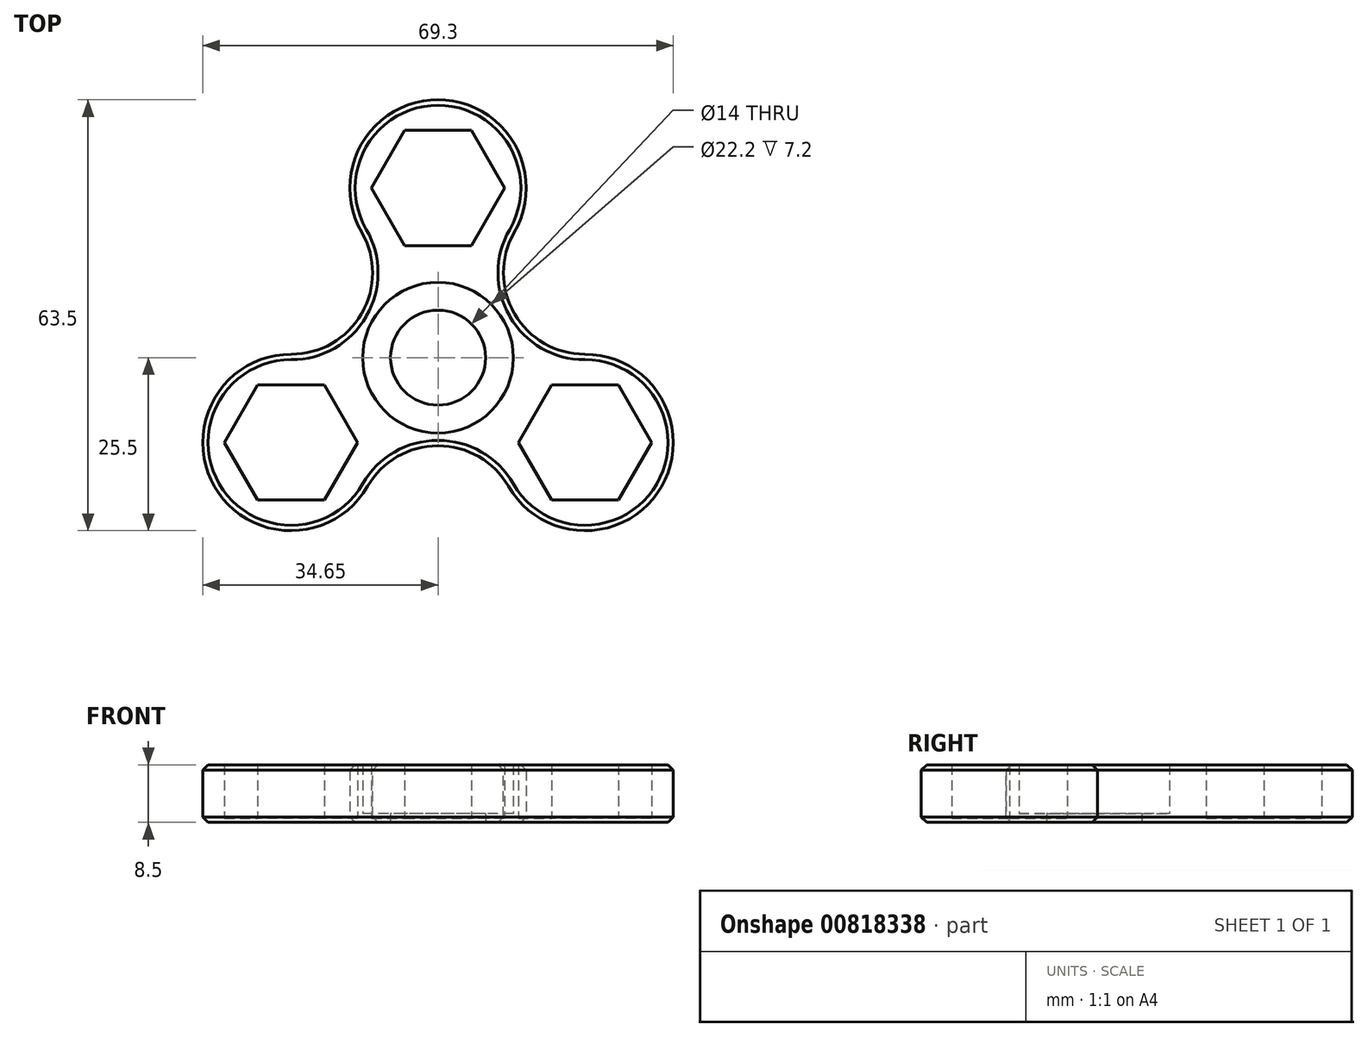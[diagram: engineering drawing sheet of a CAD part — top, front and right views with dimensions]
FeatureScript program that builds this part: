
annotation { "Feature Type Name" : "Feature", "Feature Type Description" : "" }
export const myFeature = defineFeature(function(context is Context, id is Id, definition is map)
    precondition{}
    {
        {
            var Q0;
            Q0=qCreatedBy(makeId("Top.planeOp"),FACE);
            var sketch = newSketch(context, id + "F0", { "sketchPlane" : qUnion([Q0])});
            skCircle(sketch, "E0", {"center": v(0, 0) * mm, "radius": 13 * mm});
            skCircle(sketch, "E1", {"center": v(0, 0) * mm, "radius": 11.1 * mm});
            skCircle(sketch, "E2", {"center": v(0, 25) * mm, "radius": 13 * mm});
            skCircle(sketch, "E3.cCircle", {"center": v(0, 25) * mm, "radius": 8.5 * mm, "construction": true});
            skLineSegment(sketch, "E3.0", {"start": v(9.81, 25) * mm, "end": v(4.9, 16.5) * mm});
            skLineSegment(sketch, "E3.1", {"start": v(4.9, 16.5) * mm, "end": v(-4.9, 16.5) * mm});
            skLineSegment(sketch, "E3.2", {"start": v(-4.9, 16.5) * mm, "end": v(-9.81, 25) * mm});
            skLineSegment(sketch, "E3.3", {"start": v(-9.81, 25) * mm, "end": v(-4.9, 33.5) * mm});
            skLineSegment(sketch, "E3.4", {"start": v(-4.9, 33.5) * mm, "end": v(4.9, 33.5) * mm});
            skLineSegment(sketch, "E3.5", {"start": v(4.9, 33.5) * mm, "end": v(9.81, 25) * mm});
            skPoint(sketch, "E3.0.midPoint", {"position": v(7.36, 20.75) * mm});
            skCircle(sketch, "E4", {"center": v(0, 0) * mm, "radius": 7 * mm});
            skCircle(sketch, "E5.1.0", {"center": v(-21.65, -12.5) * mm, "radius": 13 * mm});
            skLineSegment(sketch, "E5.1.1", {"start": v(-16.74, -4) * mm, "end": v(-11.84, -12.5) * mm});
            skLineSegment(sketch, "E5.1.2", {"start": v(-26.56, -4) * mm, "end": v(-16.74, -4) * mm});
            skLineSegment(sketch, "E5.1.3", {"start": v(-31.47, -12.5) * mm, "end": v(-26.56, -4) * mm});
            skLineSegment(sketch, "E5.1.4", {"start": v(-26.56, -21) * mm, "end": v(-31.47, -12.5) * mm});
            skLineSegment(sketch, "E5.1.5", {"start": v(-16.74, -21) * mm, "end": v(-26.56, -21) * mm});
            skLineSegment(sketch, "E5.1.6", {"start": v(-11.84, -12.5) * mm, "end": v(-16.74, -21) * mm});
            skCircle(sketch, "E5.2.0", {"center": v(21.65, -12.5) * mm, "radius": 13 * mm});
            skLineSegment(sketch, "E5.2.1", {"start": v(11.84, -12.5) * mm, "end": v(16.74, -4) * mm});
            skLineSegment(sketch, "E5.2.2", {"start": v(16.74, -21) * mm, "end": v(11.84, -12.5) * mm});
            skLineSegment(sketch, "E5.2.3", {"start": v(26.56, -21) * mm, "end": v(16.74, -21) * mm});
            skLineSegment(sketch, "E5.2.4", {"start": v(31.47, -12.5) * mm, "end": v(26.56, -21) * mm});
            skLineSegment(sketch, "E5.2.5", {"start": v(26.56, -4) * mm, "end": v(31.47, -12.5) * mm});
            skLineSegment(sketch, "E5.2.6", {"start": v(16.74, -4) * mm, "end": v(26.56, -4) * mm});
            skSolve(sketch);
        }
        {
            var Q0;
            Q0=makeQuery(id+"F0.imprint","IMPRINT",FACE,{"disambiguationData":[TD([[makeQuery(id+"F0.imprint","IMPRINT",EDGE,{"derivedFrom":sQuery(id+"F0.wireOp",EDGE,"E3.0")}),1.0]])]});
            var Q1;
            Q1=makeQuery(id+"F0.imprint","IMPRINT",FACE,{"disambiguationData":[TD([[makeQuery(id+"F0.imprint","IMPRINT",EDGE,{"derivedFrom":sQuery(id+"F0.wireOp",EDGE,"E3.0")}),-1.0]])]});
            var Q2;
            Q2=makeQuery(id+"F0.imprint","IMPRINT",FACE,{"disambiguationData":[TD([[makeQuery(id+"F0.imprint","IMPRINT",EDGE,{"derivedFrom":sQuery(id+"F0.wireOp",EDGE,"E1")}),1.0]])]});
            var Q3;
            Q3=makeQuery(id+"F0.imprint","IMPRINT",FACE,{"disambiguationData":[TD([[makeQuery(id+"F0.imprint","IMPRINT",EDGE,{"derivedFrom":sQuery(id+"F0.wireOp",EDGE,"E1")}),-1.0]])]});
            var Q4;
            {var subQ0=sQuery(id+"F0.wireOp",EDGE,"E2");var subQ1=sQuery(id+"F0.wireOp",EDGE,"E0");var subQ2=makeQuery(id+"F0.imprint","INTERSECT",VERTEX,{"disambiguationData":[OD(0.0)],"derivedFrom":[subQ1,subQ0]});Q4=makeQuery(id+"F0.imprint","IMPRINT",FACE,{"disambiguationData":[TD([[makeQuery(id+"F0.imprint","IMPRINT",EDGE,{"disambiguationData":[TD([[subQ2,1.0]])],"derivedFrom":subQ1}),1.0]])]});}
            var Q5;
            {var subQ0=sQuery(id+"F0.wireOp",EDGE,"d04d9439-d31e-4a44-955d-4c44843ed1f90.MirrorC");var subQ1=sQuery(id+"F0.wireOp",EDGE,"E0");var subQ2=makeQuery(id+"F0.imprint","INTERSECT",VERTEX,{"disambiguationData":[OD(0.0)],"derivedFrom":[subQ1,subQ0]});Q5=makeQuery(id+"F0.imprint","IMPRINT",FACE,{"disambiguationData":[TD([[makeQuery(id+"F0.imprint","IMPRINT",EDGE,{"disambiguationData":[TD([[subQ2,-1.0]])],"derivedFrom":subQ1}),1.0]])]});}
            var Q6;
            Q6=makeQuery(id+"F0.imprint","IMPRINT",FACE,{"disambiguationData":[TD([[makeQuery(id+"F0.imprint","IMPRINT",EDGE,{"derivedFrom":sQuery(id+"F0.wireOp",EDGE,"235c1c98-600d-46e9-b86c-8ce5ef518ee80.MirrorCS")}),-1.0]])]});
            var Q7;
            Q7=makeQuery(id+"F0.imprint","IMPRINT",FACE,{"disambiguationData":[TD([[makeQuery(id+"F0.imprint","IMPRINT",EDGE,{"derivedFrom":sQuery(id+"F0.wireOp",EDGE,"235c1c98-600d-46e9-b86c-8ce5ef518ee80.MirrorCS")}),1.0]])]});
            var Q8;
            Q8=makeQuery(id+"F0.imprint","IMPRINT",FACE,{"disambiguationData":[TD([[makeQuery(id+"F0.imprint","IMPRINT",EDGE,{"derivedFrom":sQuery(id+"F0.wireOp",EDGE,"E5.1.1")}),1.0]])]});
            var Q9;
            Q9=makeQuery(id+"F0.imprint","IMPRINT",FACE,{"disambiguationData":[TD([[makeQuery(id+"F0.imprint","IMPRINT",EDGE,{"derivedFrom":sQuery(id+"F0.wireOp",EDGE,"E5.2.1")}),1.0]])]});
            var Q10;
            Q10=makeQuery(id+"F0.imprint","IMPRINT",FACE,{"disambiguationData":[TD([[makeQuery(id+"F0.imprint","IMPRINT",EDGE,{"derivedFrom":sQuery(id+"F0.wireOp",EDGE,"E5.1.1")}),-1.0]])]});
            var Q11;
            Q11=makeQuery(id+"F0.imprint","IMPRINT",FACE,{"disambiguationData":[TD([[makeQuery(id+"F0.imprint","IMPRINT",EDGE,{"derivedFrom":sQuery(id+"F0.wireOp",EDGE,"E5.2.1")}),-1.0]])]});
            var Q12;
            {var subQ0=sQuery(id+"F0.wireOp",EDGE,"E5.1.0");var subQ1=sQuery(id+"F0.wireOp",EDGE,"E0");var subQ2=makeQuery(id+"F0.imprint","INTERSECT",VERTEX,{"disambiguationData":[OD(0.0)],"derivedFrom":[subQ1,subQ0]});Q12=makeQuery(id+"F0.imprint","IMPRINT",FACE,{"disambiguationData":[TD([[makeQuery(id+"F0.imprint","IMPRINT",EDGE,{"disambiguationData":[TD([[subQ2,-1.0]])],"derivedFrom":subQ1}),1.0]])]});}
            var Q13;
            {var subQ0=sQuery(id+"F0.wireOp",EDGE,"E5.2.0");var subQ1=sQuery(id+"F0.wireOp",EDGE,"E0");var subQ2=makeQuery(id+"F0.imprint","INTERSECT",VERTEX,{"disambiguationData":[OD(0.0)],"derivedFrom":[subQ1,subQ0]});Q13=makeQuery(id+"F0.imprint","IMPRINT",FACE,{"disambiguationData":[TD([[makeQuery(id+"F0.imprint","IMPRINT",EDGE,{"disambiguationData":[TD([[subQ2,-1.0]])],"derivedFrom":subQ1}),1.0]])]});}
            extrude(context, id + "F1", {"entities" : qUnion([Q0, Q1, Q2, Q3, Q4, Q5, Q6, Q7, Q8, Q9, Q10, Q11, Q12, Q13]), "depth" : 0.6 * mm, "offsetDistance" : 25 * mm});
        }
        {
            var Q0;
            Q0=makeQuery(id+"F0.imprint","IMPRINT",FACE,{"disambiguationData":[TD([[makeQuery(id+"F0.imprint","IMPRINT",EDGE,{"derivedFrom":sQuery(id+"F0.wireOp",EDGE,"E3.0")}),1.0]])]});
            var Q1;
            Q1=makeQuery(id+"F0.imprint","IMPRINT",FACE,{"disambiguationData":[TD([[makeQuery(id+"F0.imprint","IMPRINT",EDGE,{"derivedFrom":sQuery(id+"F0.wireOp",EDGE,"E1")}),-1.0]])]});
            var Q2;
            {var subQ0=sQuery(id+"F0.wireOp",EDGE,"E2");var subQ1=sQuery(id+"F0.wireOp",EDGE,"E0");var subQ2=makeQuery(id+"F0.imprint","INTERSECT",VERTEX,{"disambiguationData":[OD(0.0)],"derivedFrom":[subQ1,subQ0]});Q2=makeQuery(id+"F0.imprint","IMPRINT",FACE,{"disambiguationData":[TD([[makeQuery(id+"F0.imprint","IMPRINT",EDGE,{"disambiguationData":[TD([[subQ2,1.0]])],"derivedFrom":subQ1}),1.0]])]});}
            var Q3;
            {var subQ0=sQuery(id+"F0.wireOp",EDGE,"d04d9439-d31e-4a44-955d-4c44843ed1f90.MirrorC");var subQ1=sQuery(id+"F0.wireOp",EDGE,"E0");var subQ2=makeQuery(id+"F0.imprint","INTERSECT",VERTEX,{"disambiguationData":[OD(0.0)],"derivedFrom":[subQ1,subQ0]});Q3=makeQuery(id+"F0.imprint","IMPRINT",FACE,{"disambiguationData":[TD([[makeQuery(id+"F0.imprint","IMPRINT",EDGE,{"disambiguationData":[TD([[subQ2,-1.0]])],"derivedFrom":subQ1}),1.0]])]});}
            var Q4;
            Q4=makeQuery(id+"F0.imprint","IMPRINT",FACE,{"disambiguationData":[TD([[makeQuery(id+"F0.imprint","IMPRINT",EDGE,{"derivedFrom":sQuery(id+"F0.wireOp",EDGE,"235c1c98-600d-46e9-b86c-8ce5ef518ee80.MirrorCS")}),-1.0]])]});
            var Q5;
            Q5=makeQuery(id+"F0.imprint","IMPRINT",FACE,{"disambiguationData":[TD([[makeQuery(id+"F0.imprint","IMPRINT",EDGE,{"derivedFrom":sQuery(id+"F0.wireOp",EDGE,"E5.1.1")}),1.0]])]});
            var Q6;
            {var subQ0=sQuery(id+"F0.wireOp",EDGE,"E5.1.0");var subQ1=sQuery(id+"F0.wireOp",EDGE,"E0");var subQ2=makeQuery(id+"F0.imprint","INTERSECT",VERTEX,{"disambiguationData":[OD(0.0)],"derivedFrom":[subQ1,subQ0]});Q6=makeQuery(id+"F0.imprint","IMPRINT",FACE,{"disambiguationData":[TD([[makeQuery(id+"F0.imprint","IMPRINT",EDGE,{"disambiguationData":[TD([[subQ2,-1.0]])],"derivedFrom":subQ1}),1.0]])]});}
            var Q7;
            Q7=makeQuery(id+"F0.imprint","IMPRINT",FACE,{"disambiguationData":[TD([[makeQuery(id+"F0.imprint","IMPRINT",EDGE,{"derivedFrom":sQuery(id+"F0.wireOp",EDGE,"E5.2.1")}),1.0]])]});
            var Q8;
            {var subQ0=sQuery(id+"F0.wireOp",EDGE,"E5.2.0");var subQ1=sQuery(id+"F0.wireOp",EDGE,"E0");var subQ2=makeQuery(id+"F0.imprint","INTERSECT",VERTEX,{"disambiguationData":[OD(0.0)],"derivedFrom":[subQ1,subQ0]});Q8=makeQuery(id+"F0.imprint","IMPRINT",FACE,{"disambiguationData":[TD([[makeQuery(id+"F0.imprint","IMPRINT",EDGE,{"disambiguationData":[TD([[subQ2,-1.0]])],"derivedFrom":subQ1}),1.0]])]});}
            extrude(context, id + "F2", {"entities" : qUnion([Q0, Q1, Q2, Q3, Q4, Q5, Q6, Q7, Q8]), "operationType" : NewBodyOperationType.ADD, "depth" : 8.5 * mm, "offsetDistance" : 25 * mm});
        }
        {
            var Q0;
            {var subQ0=sQuery(id+"F0.wireOp",EDGE,"d04d9439-d31e-4a44-955d-4c44843ed1f90.MirrorC");var subQ1=sQuery(id+"F0.wireOp",EDGE,"E0");var subQ2=makeQuery(id+"F0.imprint","INTERSECT",VERTEX,{"disambiguationData":[OD(1.0)],"derivedFrom":[subQ1,subQ0]});Q0=makeQuery(id+"F2.boolean.opBoolean","MERGE",EDGE,{"derivedFrom":[makeQuery(id+"F1.opExtrude","SWEPT_EDGE",EDGE,{"disambiguationData":[OSD([subQ1,subQ0]),TDD([subQ2])]}),makeQuery(id+"F2.opExtrude","SWEPT_EDGE",EDGE,{"disambiguationData":[OSD([subQ1,subQ0]),TDD([subQ2])]})]});}
            var Q1;
            {var subQ0=sQuery(id+"F0.wireOp",EDGE,"E2");var subQ1=sQuery(id+"F0.wireOp",EDGE,"E0");var subQ2=makeQuery(id+"F0.imprint","INTERSECT",VERTEX,{"disambiguationData":[OD(1.0)],"derivedFrom":[subQ1,subQ0]});Q1=makeQuery(id+"F2.boolean.opBoolean","MERGE",EDGE,{"derivedFrom":[makeQuery(id+"F1.opExtrude","SWEPT_EDGE",EDGE,{"disambiguationData":[OSD([subQ1,subQ0]),TDD([subQ2])]}),makeQuery(id+"F2.opExtrude","SWEPT_EDGE",EDGE,{"disambiguationData":[OSD([subQ1,subQ0]),TDD([subQ2])]})]});}
            var Q2;
            {var subQ0=sQuery(id+"F0.wireOp",EDGE,"E2");var subQ1=sQuery(id+"F0.wireOp",EDGE,"E0");var subQ2=makeQuery(id+"F0.imprint","INTERSECT",VERTEX,{"disambiguationData":[OD(0.0)],"derivedFrom":[subQ1,subQ0]});Q2=makeQuery(id+"F2.boolean.opBoolean","MERGE",EDGE,{"derivedFrom":[makeQuery(id+"F1.opExtrude","SWEPT_EDGE",EDGE,{"disambiguationData":[OSD([subQ1,subQ0]),TDD([subQ2])]}),makeQuery(id+"F2.opExtrude","SWEPT_EDGE",EDGE,{"disambiguationData":[OSD([subQ1,subQ0]),TDD([subQ2])]})]});}
            var Q3;
            {var subQ0=sQuery(id+"F0.wireOp",EDGE,"d04d9439-d31e-4a44-955d-4c44843ed1f90.MirrorC");var subQ1=sQuery(id+"F0.wireOp",EDGE,"E0");var subQ2=makeQuery(id+"F0.imprint","INTERSECT",VERTEX,{"disambiguationData":[OD(0.0)],"derivedFrom":[subQ1,subQ0]});Q3=makeQuery(id+"F2.boolean.opBoolean","MERGE",EDGE,{"derivedFrom":[makeQuery(id+"F1.opExtrude","SWEPT_EDGE",EDGE,{"disambiguationData":[OSD([subQ1,subQ0]),TDD([subQ2])]}),makeQuery(id+"F2.opExtrude","SWEPT_EDGE",EDGE,{"disambiguationData":[OSD([subQ1,subQ0]),TDD([subQ2])]})]});}
            var Q4;
            {var subQ0=sQuery(id+"F0.wireOp",EDGE,"E5.1.0");var subQ1=sQuery(id+"F0.wireOp",EDGE,"E0");var subQ2=makeQuery(id+"F0.imprint","INTERSECT",VERTEX,{"disambiguationData":[OD(0.0)],"derivedFrom":[subQ1,subQ0]});Q4=makeQuery(id+"F2.boolean.opBoolean","MERGE",EDGE,{"derivedFrom":[makeQuery(id+"F1.opExtrude","SWEPT_EDGE",EDGE,{"disambiguationData":[OSD([subQ1,subQ0]),TDD([subQ2])]}),makeQuery(id+"F2.opExtrude","SWEPT_EDGE",EDGE,{"disambiguationData":[OSD([subQ1,subQ0]),TDD([subQ2])]})]});}
            var Q5;
            {var subQ0=sQuery(id+"F0.wireOp",EDGE,"E5.1.0");var subQ1=sQuery(id+"F0.wireOp",EDGE,"E0");var subQ2=makeQuery(id+"F0.imprint","INTERSECT",VERTEX,{"disambiguationData":[OD(1.0)],"derivedFrom":[subQ1,subQ0]});Q5=makeQuery(id+"F2.boolean.opBoolean","MERGE",EDGE,{"derivedFrom":[makeQuery(id+"F1.opExtrude","SWEPT_EDGE",EDGE,{"disambiguationData":[OSD([subQ1,subQ0]),TDD([subQ2])]}),makeQuery(id+"F2.opExtrude","SWEPT_EDGE",EDGE,{"disambiguationData":[OSD([subQ1,subQ0]),TDD([subQ2])]})]});}
            var Q6;
            {var subQ0=sQuery(id+"F0.wireOp",EDGE,"E5.2.0");var subQ1=sQuery(id+"F0.wireOp",EDGE,"E0");var subQ2=makeQuery(id+"F0.imprint","INTERSECT",VERTEX,{"disambiguationData":[OD(0.0)],"derivedFrom":[subQ1,subQ0]});Q6=makeQuery(id+"F2.boolean.opBoolean","MERGE",EDGE,{"derivedFrom":[makeQuery(id+"F1.opExtrude","SWEPT_EDGE",EDGE,{"disambiguationData":[OSD([subQ1,subQ0]),TDD([subQ2])]}),makeQuery(id+"F2.opExtrude","SWEPT_EDGE",EDGE,{"disambiguationData":[OSD([subQ1,subQ0]),TDD([subQ2])]})]});}
            var Q7;
            {var subQ0=sQuery(id+"F0.wireOp",EDGE,"E5.2.0");var subQ1=sQuery(id+"F0.wireOp",EDGE,"E0");var subQ2=makeQuery(id+"F0.imprint","INTERSECT",VERTEX,{"disambiguationData":[OD(1.0)],"derivedFrom":[subQ1,subQ0]});Q7=makeQuery(id+"F2.boolean.opBoolean","MERGE",EDGE,{"derivedFrom":[makeQuery(id+"F1.opExtrude","SWEPT_EDGE",EDGE,{"disambiguationData":[OSD([subQ1,subQ0]),TDD([subQ2])]}),makeQuery(id+"F2.opExtrude","SWEPT_EDGE",EDGE,{"disambiguationData":[OSD([subQ1,subQ0]),TDD([subQ2])]})]});}
            fillet(context, id + "F3", {"entities" : qUnion([Q0, Q1, Q2, Q3, Q4, Q5, Q6, Q7]), "radius" : 11.85 * mm, "tangentPropagation" : true, "allowEdgeOverflow" : false});
        }
        {
            var Q0;
            Q0=makeQuery(id+"F2.opExtrude","CAP_EDGE",EDGE,{"disambiguationData":[OSD([sQuery(id+"F0.wireOp",EDGE,"d04d9439-d31e-4a44-955d-4c44843ed1f90.MirrorC")])],"isStart":false});
            var Q1;
            {var subQ0=sQuery(id+"F0.wireOp",EDGE,"d04d9439-d31e-4a44-955d-4c44843ed1f90.MirrorC");var subQ1=sQuery(id+"F0.wireOp",EDGE,"E0");var subQ2=makeQuery(id+"F0.imprint","INTERSECT",VERTEX,{"disambiguationData":[OD(1.0)],"derivedFrom":[subQ1,subQ0]});Q1=makeQuery(id+"F3.opFillet","BLEND_EDGE",EDGE,{"blendedFrom":[makeQuery(id+"F2.boolean.opBoolean","MERGE",EDGE,{"derivedFrom":[makeQuery(id+"F1.opExtrude","SWEPT_EDGE",EDGE,{"disambiguationData":[OSD([subQ1,subQ0]),TDD([subQ2])]}),makeQuery(id+"F2.opExtrude","SWEPT_EDGE",EDGE,{"disambiguationData":[OSD([subQ1,subQ0]),TDD([subQ2])]})]}),makeQuery(id+"F2.opExtrude","CAP_FACE",FACE,{"disambiguationData":[OSD([subQ1,sQuery(id+"F0.wireOp",EDGE,"E1"),sQuery(id+"F0.wireOp",EDGE,"E2"),sQuery(id+"F0.wireOp",EDGE,"E3.0"),sQuery(id+"F0.wireOp",EDGE,"E3.1"),sQuery(id+"F0.wireOp",EDGE,"E3.2"),sQuery(id+"F0.wireOp",EDGE,"E3.3"),sQuery(id+"F0.wireOp",EDGE,"E3.4"),sQuery(id+"F0.wireOp",EDGE,"E3.5"),subQ0,sQuery(id+"F0.wireOp",EDGE,"235c1c98-600d-46e9-b86c-8ce5ef518ee80.MirrorCS"),sQuery(id+"F0.wireOp",EDGE,"621068df-2c1f-45c7-b7be-a557bf321d120.MirrorCS"),sQuery(id+"F0.wireOp",EDGE,"25bd9b63-27a9-48e3-be2a-9a611c17aff90.MirrorCS"),sQuery(id+"F0.wireOp",EDGE,"6dd50a28-7f5a-452d-aca2-9bb57bd0a7700.MirrorCS"),sQuery(id+"F0.wireOp",EDGE,"15785d12-83de-4acf-9477-1c0fc410dcc50.MirrorCS"),sQuery(id+"F0.wireOp",EDGE,"e7483691-f99c-4309-b820-2ef5816a8e4c0.MirrorCS")])],"isStart":false})],"blendedInto":[makeQuery(id+"F2.opExtrude","CAP_FACE",FACE,{"disambiguationData":[OSD([subQ1,sQuery(id+"F0.wireOp",EDGE,"E1"),sQuery(id+"F0.wireOp",EDGE,"E2"),sQuery(id+"F0.wireOp",EDGE,"E3.0"),sQuery(id+"F0.wireOp",EDGE,"E3.1"),sQuery(id+"F0.wireOp",EDGE,"E3.2"),sQuery(id+"F0.wireOp",EDGE,"E3.3"),sQuery(id+"F0.wireOp",EDGE,"E3.4"),sQuery(id+"F0.wireOp",EDGE,"E3.5"),subQ0,sQuery(id+"F0.wireOp",EDGE,"235c1c98-600d-46e9-b86c-8ce5ef518ee80.MirrorCS"),sQuery(id+"F0.wireOp",EDGE,"621068df-2c1f-45c7-b7be-a557bf321d120.MirrorCS"),sQuery(id+"F0.wireOp",EDGE,"25bd9b63-27a9-48e3-be2a-9a611c17aff90.MirrorCS"),sQuery(id+"F0.wireOp",EDGE,"6dd50a28-7f5a-452d-aca2-9bb57bd0a7700.MirrorCS"),sQuery(id+"F0.wireOp",EDGE,"15785d12-83de-4acf-9477-1c0fc410dcc50.MirrorCS"),sQuery(id+"F0.wireOp",EDGE,"e7483691-f99c-4309-b820-2ef5816a8e4c0.MirrorCS")])],"isStart":false})]});}
            var Q2;
            {var subQ0=sQuery(id+"F0.wireOp",EDGE,"E0");Q2=makeQuery(id+"F2.opExtrude","CAP_EDGE",EDGE,{"disambiguationData":[OSD([subQ0]),TDD([makeQuery(id+"F0.imprint","IMPRINT",EDGE,{"disambiguationData":[TD([[makeQuery(id+"F0.imprint","INTERSECT",VERTEX,{"disambiguationData":[OD(1.0)],"derivedFrom":[subQ0,sQuery(id+"F0.wireOp",EDGE,"E2")]}),1.0]])],"derivedFrom":subQ0})])],"isStart":false});}
            var Q3;
            {var subQ0=sQuery(id+"F0.wireOp",EDGE,"E2");var subQ1=sQuery(id+"F0.wireOp",EDGE,"E0");var subQ2=makeQuery(id+"F0.imprint","INTERSECT",VERTEX,{"disambiguationData":[OD(1.0)],"derivedFrom":[subQ1,subQ0]});Q3=makeQuery(id+"F3.opFillet","BLEND_EDGE",EDGE,{"blendedFrom":[makeQuery(id+"F2.boolean.opBoolean","MERGE",EDGE,{"derivedFrom":[makeQuery(id+"F1.opExtrude","SWEPT_EDGE",EDGE,{"disambiguationData":[OSD([subQ1,subQ0]),TDD([subQ2])]}),makeQuery(id+"F2.opExtrude","SWEPT_EDGE",EDGE,{"disambiguationData":[OSD([subQ1,subQ0]),TDD([subQ2])]})]}),makeQuery(id+"F2.opExtrude","CAP_FACE",FACE,{"disambiguationData":[OSD([subQ1,sQuery(id+"F0.wireOp",EDGE,"E1"),subQ0,sQuery(id+"F0.wireOp",EDGE,"E3.0"),sQuery(id+"F0.wireOp",EDGE,"E3.1"),sQuery(id+"F0.wireOp",EDGE,"E3.2"),sQuery(id+"F0.wireOp",EDGE,"E3.3"),sQuery(id+"F0.wireOp",EDGE,"E3.4"),sQuery(id+"F0.wireOp",EDGE,"E3.5"),sQuery(id+"F0.wireOp",EDGE,"d04d9439-d31e-4a44-955d-4c44843ed1f90.MirrorC"),sQuery(id+"F0.wireOp",EDGE,"235c1c98-600d-46e9-b86c-8ce5ef518ee80.MirrorCS"),sQuery(id+"F0.wireOp",EDGE,"621068df-2c1f-45c7-b7be-a557bf321d120.MirrorCS"),sQuery(id+"F0.wireOp",EDGE,"25bd9b63-27a9-48e3-be2a-9a611c17aff90.MirrorCS"),sQuery(id+"F0.wireOp",EDGE,"6dd50a28-7f5a-452d-aca2-9bb57bd0a7700.MirrorCS"),sQuery(id+"F0.wireOp",EDGE,"15785d12-83de-4acf-9477-1c0fc410dcc50.MirrorCS"),sQuery(id+"F0.wireOp",EDGE,"e7483691-f99c-4309-b820-2ef5816a8e4c0.MirrorCS")])],"isStart":false})],"blendedInto":[makeQuery(id+"F2.opExtrude","CAP_FACE",FACE,{"disambiguationData":[OSD([subQ1,sQuery(id+"F0.wireOp",EDGE,"E1"),subQ0,sQuery(id+"F0.wireOp",EDGE,"E3.0"),sQuery(id+"F0.wireOp",EDGE,"E3.1"),sQuery(id+"F0.wireOp",EDGE,"E3.2"),sQuery(id+"F0.wireOp",EDGE,"E3.3"),sQuery(id+"F0.wireOp",EDGE,"E3.4"),sQuery(id+"F0.wireOp",EDGE,"E3.5"),sQuery(id+"F0.wireOp",EDGE,"d04d9439-d31e-4a44-955d-4c44843ed1f90.MirrorC"),sQuery(id+"F0.wireOp",EDGE,"235c1c98-600d-46e9-b86c-8ce5ef518ee80.MirrorCS"),sQuery(id+"F0.wireOp",EDGE,"621068df-2c1f-45c7-b7be-a557bf321d120.MirrorCS"),sQuery(id+"F0.wireOp",EDGE,"25bd9b63-27a9-48e3-be2a-9a611c17aff90.MirrorCS"),sQuery(id+"F0.wireOp",EDGE,"6dd50a28-7f5a-452d-aca2-9bb57bd0a7700.MirrorCS"),sQuery(id+"F0.wireOp",EDGE,"15785d12-83de-4acf-9477-1c0fc410dcc50.MirrorCS"),sQuery(id+"F0.wireOp",EDGE,"e7483691-f99c-4309-b820-2ef5816a8e4c0.MirrorCS")])],"isStart":false})]});}
            var Q4;
            Q4=makeQuery(id+"F2.opExtrude","CAP_EDGE",EDGE,{"disambiguationData":[OSD([sQuery(id+"F0.wireOp",EDGE,"E2")])],"isStart":false});
            var Q5;
            {var subQ0=sQuery(id+"F0.wireOp",EDGE,"E2");var subQ1=sQuery(id+"F0.wireOp",EDGE,"E0");var subQ2=makeQuery(id+"F0.imprint","INTERSECT",VERTEX,{"disambiguationData":[OD(0.0)],"derivedFrom":[subQ1,subQ0]});Q5=makeQuery(id+"F3.opFillet","BLEND_EDGE",EDGE,{"blendedFrom":[makeQuery(id+"F2.boolean.opBoolean","MERGE",EDGE,{"derivedFrom":[makeQuery(id+"F1.opExtrude","SWEPT_EDGE",EDGE,{"disambiguationData":[OSD([subQ1,subQ0]),TDD([subQ2])]}),makeQuery(id+"F2.opExtrude","SWEPT_EDGE",EDGE,{"disambiguationData":[OSD([subQ1,subQ0]),TDD([subQ2])]})]}),makeQuery(id+"F2.opExtrude","CAP_FACE",FACE,{"disambiguationData":[OSD([subQ1,sQuery(id+"F0.wireOp",EDGE,"E1"),subQ0,sQuery(id+"F0.wireOp",EDGE,"E3.0"),sQuery(id+"F0.wireOp",EDGE,"E3.1"),sQuery(id+"F0.wireOp",EDGE,"E3.2"),sQuery(id+"F0.wireOp",EDGE,"E3.3"),sQuery(id+"F0.wireOp",EDGE,"E3.4"),sQuery(id+"F0.wireOp",EDGE,"E3.5"),sQuery(id+"F0.wireOp",EDGE,"d04d9439-d31e-4a44-955d-4c44843ed1f90.MirrorC"),sQuery(id+"F0.wireOp",EDGE,"235c1c98-600d-46e9-b86c-8ce5ef518ee80.MirrorCS"),sQuery(id+"F0.wireOp",EDGE,"621068df-2c1f-45c7-b7be-a557bf321d120.MirrorCS"),sQuery(id+"F0.wireOp",EDGE,"25bd9b63-27a9-48e3-be2a-9a611c17aff90.MirrorCS"),sQuery(id+"F0.wireOp",EDGE,"6dd50a28-7f5a-452d-aca2-9bb57bd0a7700.MirrorCS"),sQuery(id+"F0.wireOp",EDGE,"15785d12-83de-4acf-9477-1c0fc410dcc50.MirrorCS"),sQuery(id+"F0.wireOp",EDGE,"e7483691-f99c-4309-b820-2ef5816a8e4c0.MirrorCS")])],"isStart":false})],"blendedInto":[makeQuery(id+"F2.opExtrude","CAP_FACE",FACE,{"disambiguationData":[OSD([subQ1,sQuery(id+"F0.wireOp",EDGE,"E1"),subQ0,sQuery(id+"F0.wireOp",EDGE,"E3.0"),sQuery(id+"F0.wireOp",EDGE,"E3.1"),sQuery(id+"F0.wireOp",EDGE,"E3.2"),sQuery(id+"F0.wireOp",EDGE,"E3.3"),sQuery(id+"F0.wireOp",EDGE,"E3.4"),sQuery(id+"F0.wireOp",EDGE,"E3.5"),sQuery(id+"F0.wireOp",EDGE,"d04d9439-d31e-4a44-955d-4c44843ed1f90.MirrorC"),sQuery(id+"F0.wireOp",EDGE,"235c1c98-600d-46e9-b86c-8ce5ef518ee80.MirrorCS"),sQuery(id+"F0.wireOp",EDGE,"621068df-2c1f-45c7-b7be-a557bf321d120.MirrorCS"),sQuery(id+"F0.wireOp",EDGE,"25bd9b63-27a9-48e3-be2a-9a611c17aff90.MirrorCS"),sQuery(id+"F0.wireOp",EDGE,"6dd50a28-7f5a-452d-aca2-9bb57bd0a7700.MirrorCS"),sQuery(id+"F0.wireOp",EDGE,"15785d12-83de-4acf-9477-1c0fc410dcc50.MirrorCS"),sQuery(id+"F0.wireOp",EDGE,"e7483691-f99c-4309-b820-2ef5816a8e4c0.MirrorCS")])],"isStart":false})]});}
            var Q6;
            {var subQ0=sQuery(id+"F0.wireOp",EDGE,"E0");Q6=makeQuery(id+"F2.opExtrude","CAP_EDGE",EDGE,{"disambiguationData":[OSD([subQ0]),TDD([makeQuery(id+"F0.imprint","IMPRINT",EDGE,{"disambiguationData":[TD([[makeQuery(id+"F0.imprint","INTERSECT",VERTEX,{"disambiguationData":[OD(0.0)],"derivedFrom":[subQ0,sQuery(id+"F0.wireOp",EDGE,"E2")]}),-1.0]])],"derivedFrom":subQ0})])],"isStart":false});}
            var Q7;
            {var subQ0=sQuery(id+"F0.wireOp",EDGE,"d04d9439-d31e-4a44-955d-4c44843ed1f90.MirrorC");var subQ1=sQuery(id+"F0.wireOp",EDGE,"E0");var subQ2=makeQuery(id+"F0.imprint","INTERSECT",VERTEX,{"disambiguationData":[OD(0.0)],"derivedFrom":[subQ1,subQ0]});Q7=makeQuery(id+"F3.opFillet","BLEND_EDGE",EDGE,{"blendedFrom":[makeQuery(id+"F2.boolean.opBoolean","MERGE",EDGE,{"derivedFrom":[makeQuery(id+"F1.opExtrude","SWEPT_EDGE",EDGE,{"disambiguationData":[OSD([subQ1,subQ0]),TDD([subQ2])]}),makeQuery(id+"F2.opExtrude","SWEPT_EDGE",EDGE,{"disambiguationData":[OSD([subQ1,subQ0]),TDD([subQ2])]})]}),makeQuery(id+"F2.opExtrude","CAP_FACE",FACE,{"disambiguationData":[OSD([subQ1,sQuery(id+"F0.wireOp",EDGE,"E1"),sQuery(id+"F0.wireOp",EDGE,"E2"),sQuery(id+"F0.wireOp",EDGE,"E3.0"),sQuery(id+"F0.wireOp",EDGE,"E3.1"),sQuery(id+"F0.wireOp",EDGE,"E3.2"),sQuery(id+"F0.wireOp",EDGE,"E3.3"),sQuery(id+"F0.wireOp",EDGE,"E3.4"),sQuery(id+"F0.wireOp",EDGE,"E3.5"),subQ0,sQuery(id+"F0.wireOp",EDGE,"235c1c98-600d-46e9-b86c-8ce5ef518ee80.MirrorCS"),sQuery(id+"F0.wireOp",EDGE,"621068df-2c1f-45c7-b7be-a557bf321d120.MirrorCS"),sQuery(id+"F0.wireOp",EDGE,"25bd9b63-27a9-48e3-be2a-9a611c17aff90.MirrorCS"),sQuery(id+"F0.wireOp",EDGE,"6dd50a28-7f5a-452d-aca2-9bb57bd0a7700.MirrorCS"),sQuery(id+"F0.wireOp",EDGE,"15785d12-83de-4acf-9477-1c0fc410dcc50.MirrorCS"),sQuery(id+"F0.wireOp",EDGE,"e7483691-f99c-4309-b820-2ef5816a8e4c0.MirrorCS")])],"isStart":false})],"blendedInto":[makeQuery(id+"F2.opExtrude","CAP_FACE",FACE,{"disambiguationData":[OSD([subQ1,sQuery(id+"F0.wireOp",EDGE,"E1"),sQuery(id+"F0.wireOp",EDGE,"E2"),sQuery(id+"F0.wireOp",EDGE,"E3.0"),sQuery(id+"F0.wireOp",EDGE,"E3.1"),sQuery(id+"F0.wireOp",EDGE,"E3.2"),sQuery(id+"F0.wireOp",EDGE,"E3.3"),sQuery(id+"F0.wireOp",EDGE,"E3.4"),sQuery(id+"F0.wireOp",EDGE,"E3.5"),subQ0,sQuery(id+"F0.wireOp",EDGE,"235c1c98-600d-46e9-b86c-8ce5ef518ee80.MirrorCS"),sQuery(id+"F0.wireOp",EDGE,"621068df-2c1f-45c7-b7be-a557bf321d120.MirrorCS"),sQuery(id+"F0.wireOp",EDGE,"25bd9b63-27a9-48e3-be2a-9a611c17aff90.MirrorCS"),sQuery(id+"F0.wireOp",EDGE,"6dd50a28-7f5a-452d-aca2-9bb57bd0a7700.MirrorCS"),sQuery(id+"F0.wireOp",EDGE,"15785d12-83de-4acf-9477-1c0fc410dcc50.MirrorCS"),sQuery(id+"F0.wireOp",EDGE,"e7483691-f99c-4309-b820-2ef5816a8e4c0.MirrorCS")])],"isStart":false})]});}
            var Q8;
            Q8=makeQuery(id+"F1.opExtrude","CAP_EDGE",EDGE,{"disambiguationData":[OSD([sQuery(id+"F0.wireOp",EDGE,"d04d9439-d31e-4a44-955d-4c44843ed1f90.MirrorC")])],"isStart":true});
            var Q9;
            {var subQ0=sQuery(id+"F0.wireOp",EDGE,"d04d9439-d31e-4a44-955d-4c44843ed1f90.MirrorC");var subQ1=sQuery(id+"F0.wireOp",EDGE,"E0");var subQ2=makeQuery(id+"F0.imprint","INTERSECT",VERTEX,{"disambiguationData":[OD(0.0)],"derivedFrom":[subQ1,subQ0]});Q9=makeQuery(id+"F3.opFillet","BLEND_EDGE",EDGE,{"blendedFrom":[makeQuery(id+"F2.boolean.opBoolean","MERGE",EDGE,{"derivedFrom":[makeQuery(id+"F1.opExtrude","SWEPT_EDGE",EDGE,{"disambiguationData":[OSD([subQ1,subQ0]),TDD([subQ2])]}),makeQuery(id+"F2.opExtrude","SWEPT_EDGE",EDGE,{"disambiguationData":[OSD([subQ1,subQ0]),TDD([subQ2])]})]}),makeQuery(id+"F1.opExtrude","CAP_FACE",FACE,{"disambiguationData":[OSD([subQ1,sQuery(id+"F0.wireOp",EDGE,"E2"),subQ0,sQuery(id+"F0.wireOp",EDGE,"E4")])],"isStart":true})],"blendedInto":[makeQuery(id+"F1.opExtrude","CAP_FACE",FACE,{"disambiguationData":[OSD([subQ1,sQuery(id+"F0.wireOp",EDGE,"E2"),subQ0,sQuery(id+"F0.wireOp",EDGE,"E4")])],"isStart":true})]});}
            var Q10;
            {var subQ0=sQuery(id+"F0.wireOp",EDGE,"E0");Q10=makeQuery(id+"F1.opExtrude","CAP_EDGE",EDGE,{"disambiguationData":[OSD([subQ0]),TDD([makeQuery(id+"F0.imprint","IMPRINT",EDGE,{"disambiguationData":[TD([[makeQuery(id+"F0.imprint","INTERSECT",VERTEX,{"disambiguationData":[OD(0.0)],"derivedFrom":[subQ0,sQuery(id+"F0.wireOp",EDGE,"E2")]}),-1.0]])],"derivedFrom":subQ0})])],"isStart":true});}
            var Q11;
            {var subQ0=sQuery(id+"F0.wireOp",EDGE,"E2");var subQ1=sQuery(id+"F0.wireOp",EDGE,"E0");var subQ2=makeQuery(id+"F0.imprint","INTERSECT",VERTEX,{"disambiguationData":[OD(0.0)],"derivedFrom":[subQ1,subQ0]});Q11=makeQuery(id+"F3.opFillet","BLEND_EDGE",EDGE,{"blendedFrom":[makeQuery(id+"F2.boolean.opBoolean","MERGE",EDGE,{"derivedFrom":[makeQuery(id+"F1.opExtrude","SWEPT_EDGE",EDGE,{"disambiguationData":[OSD([subQ1,subQ0]),TDD([subQ2])]}),makeQuery(id+"F2.opExtrude","SWEPT_EDGE",EDGE,{"disambiguationData":[OSD([subQ1,subQ0]),TDD([subQ2])]})]}),makeQuery(id+"F1.opExtrude","CAP_FACE",FACE,{"disambiguationData":[OSD([subQ1,subQ0,sQuery(id+"F0.wireOp",EDGE,"d04d9439-d31e-4a44-955d-4c44843ed1f90.MirrorC"),sQuery(id+"F0.wireOp",EDGE,"E4")])],"isStart":true})],"blendedInto":[makeQuery(id+"F1.opExtrude","CAP_FACE",FACE,{"disambiguationData":[OSD([subQ1,subQ0,sQuery(id+"F0.wireOp",EDGE,"d04d9439-d31e-4a44-955d-4c44843ed1f90.MirrorC"),sQuery(id+"F0.wireOp",EDGE,"E4")])],"isStart":true})]});}
            var Q12;
            Q12=makeQuery(id+"F1.opExtrude","CAP_EDGE",EDGE,{"disambiguationData":[OSD([sQuery(id+"F0.wireOp",EDGE,"E2")])],"isStart":true});
            var Q13;
            {var subQ0=sQuery(id+"F0.wireOp",EDGE,"E2");var subQ1=sQuery(id+"F0.wireOp",EDGE,"E0");var subQ2=makeQuery(id+"F0.imprint","INTERSECT",VERTEX,{"disambiguationData":[OD(1.0)],"derivedFrom":[subQ1,subQ0]});Q13=makeQuery(id+"F3.opFillet","BLEND_EDGE",EDGE,{"blendedFrom":[makeQuery(id+"F2.boolean.opBoolean","MERGE",EDGE,{"derivedFrom":[makeQuery(id+"F1.opExtrude","SWEPT_EDGE",EDGE,{"disambiguationData":[OSD([subQ1,subQ0]),TDD([subQ2])]}),makeQuery(id+"F2.opExtrude","SWEPT_EDGE",EDGE,{"disambiguationData":[OSD([subQ1,subQ0]),TDD([subQ2])]})]}),makeQuery(id+"F1.opExtrude","CAP_FACE",FACE,{"disambiguationData":[OSD([subQ1,subQ0,sQuery(id+"F0.wireOp",EDGE,"d04d9439-d31e-4a44-955d-4c44843ed1f90.MirrorC"),sQuery(id+"F0.wireOp",EDGE,"E4")])],"isStart":true})],"blendedInto":[makeQuery(id+"F1.opExtrude","CAP_FACE",FACE,{"disambiguationData":[OSD([subQ1,subQ0,sQuery(id+"F0.wireOp",EDGE,"d04d9439-d31e-4a44-955d-4c44843ed1f90.MirrorC"),sQuery(id+"F0.wireOp",EDGE,"E4")])],"isStart":true})]});}
            var Q14;
            {var subQ0=sQuery(id+"F0.wireOp",EDGE,"E0");Q14=makeQuery(id+"F1.opExtrude","CAP_EDGE",EDGE,{"disambiguationData":[OSD([subQ0]),TDD([makeQuery(id+"F0.imprint","IMPRINT",EDGE,{"disambiguationData":[TD([[makeQuery(id+"F0.imprint","INTERSECT",VERTEX,{"disambiguationData":[OD(1.0)],"derivedFrom":[subQ0,sQuery(id+"F0.wireOp",EDGE,"E2")]}),1.0]])],"derivedFrom":subQ0})])],"isStart":true});}
            var Q15;
            {var subQ0=sQuery(id+"F0.wireOp",EDGE,"d04d9439-d31e-4a44-955d-4c44843ed1f90.MirrorC");var subQ1=sQuery(id+"F0.wireOp",EDGE,"E0");var subQ2=makeQuery(id+"F0.imprint","INTERSECT",VERTEX,{"disambiguationData":[OD(1.0)],"derivedFrom":[subQ1,subQ0]});Q15=makeQuery(id+"F3.opFillet","BLEND_EDGE",EDGE,{"blendedFrom":[makeQuery(id+"F2.boolean.opBoolean","MERGE",EDGE,{"derivedFrom":[makeQuery(id+"F1.opExtrude","SWEPT_EDGE",EDGE,{"disambiguationData":[OSD([subQ1,subQ0]),TDD([subQ2])]}),makeQuery(id+"F2.opExtrude","SWEPT_EDGE",EDGE,{"disambiguationData":[OSD([subQ1,subQ0]),TDD([subQ2])]})]}),makeQuery(id+"F1.opExtrude","CAP_FACE",FACE,{"disambiguationData":[OSD([subQ1,sQuery(id+"F0.wireOp",EDGE,"E2"),subQ0,sQuery(id+"F0.wireOp",EDGE,"E4")])],"isStart":true})],"blendedInto":[makeQuery(id+"F1.opExtrude","CAP_FACE",FACE,{"disambiguationData":[OSD([subQ1,sQuery(id+"F0.wireOp",EDGE,"E2"),subQ0,sQuery(id+"F0.wireOp",EDGE,"E4")])],"isStart":true})]});}
            chamfer(context, id + "F4", {"entities" : qUnion([Q0, Q1, Q2, Q3, Q4, Q5, Q6, Q7, Q8, Q9, Q10, Q11, Q12, Q13, Q14, Q15]), "width" : 0.8 * mm, "tangentPropagation" : true});
        }
        {
            var Q0;
            Q0=makeQuery(id+"F0.imprint","IMPRINT",FACE,{"disambiguationData":[TD([[makeQuery(id+"F0.imprint","IMPRINT",EDGE,{"derivedFrom":sQuery(id+"F0.wireOp",EDGE,"E1")}),1.0]])]});
            extrude(context, id + "F5", {"entities" : qUnion([Q0]), "operationType" : NewBodyOperationType.ADD, "depth" : 1.3 * mm, "offsetDistance" : 25 * mm});
        }
    });
